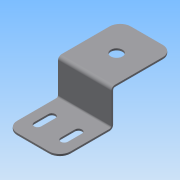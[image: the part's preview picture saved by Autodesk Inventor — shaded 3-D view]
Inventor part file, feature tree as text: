
AUTODESK INVENTOR PART (.ipt)
format: ipt  version: 2016 (Build 200138000, 138)  size: 140,800 bytes
history: native  units: mm
features: other x11, sketch x4, hole x1, extrude x1
ambient origin geometry x8: Origin, YZ Plane, XZ Plane, XY Plane, X Axis, Y Axis, Z Axis, Center Point
bodies: Volumenkörper1 (feature_tree)
feature tree (17):
  other  "Fläche1"
  other  "Lasche1"
  other  "Lasche2"
  hole  "Bohrung2"  [1 undecoded]
  extrude  "Extrusion2"  Depth=1.0mm
  other  "Eckenrundung1"
  sketch  "Skizze1"  dims[d0=30.0mm d1=30.0mm]
  other  "Grobblech1"
  sketch  "Skizze2"  dims[d2=1.0mm d3=1.0mm]
  other  "Grobblech2"
  other  "Biegung1"
  other  "Ecke1"
  sketch  "Skizze3"  dims[d4=0.5mm]
  other  "Grobblech3"
  other  "Biegung2"
  other  "Ecke2"
  sketch  "Skizze6"  dims[d5=2.0mm d6=1.0mm d7=20.0mm d8=90.0deg d9=1.0mm d10=4.0mm d11=1.0mm d12=1.0mm d13=1.0mm d14=0.5mm d15=2.0mm d16=1.0mm d17=34.0mm d18=90.0deg d19=1.0mm d20=4.0mm d21=1.0mm d22=1.0mm d38=17.0mm d49=1.0mm d40=6.6mm d41=6.0mm d42=4.0mm d43=2.0mm d44=90.0deg d45=1.0mm d46=20.594885mm d47=15.0mm d48=12.0mm d50=4.0mm d51=10.0mm d52=0.0mm d53=6.0mm d31=1.0mm d32=1.0mm]
note: 1 required parameter value undecoded (feature->parameter linkage not recoverable at this tier; creation-order binding heuristic only, values carry confidence <= 0.55)
